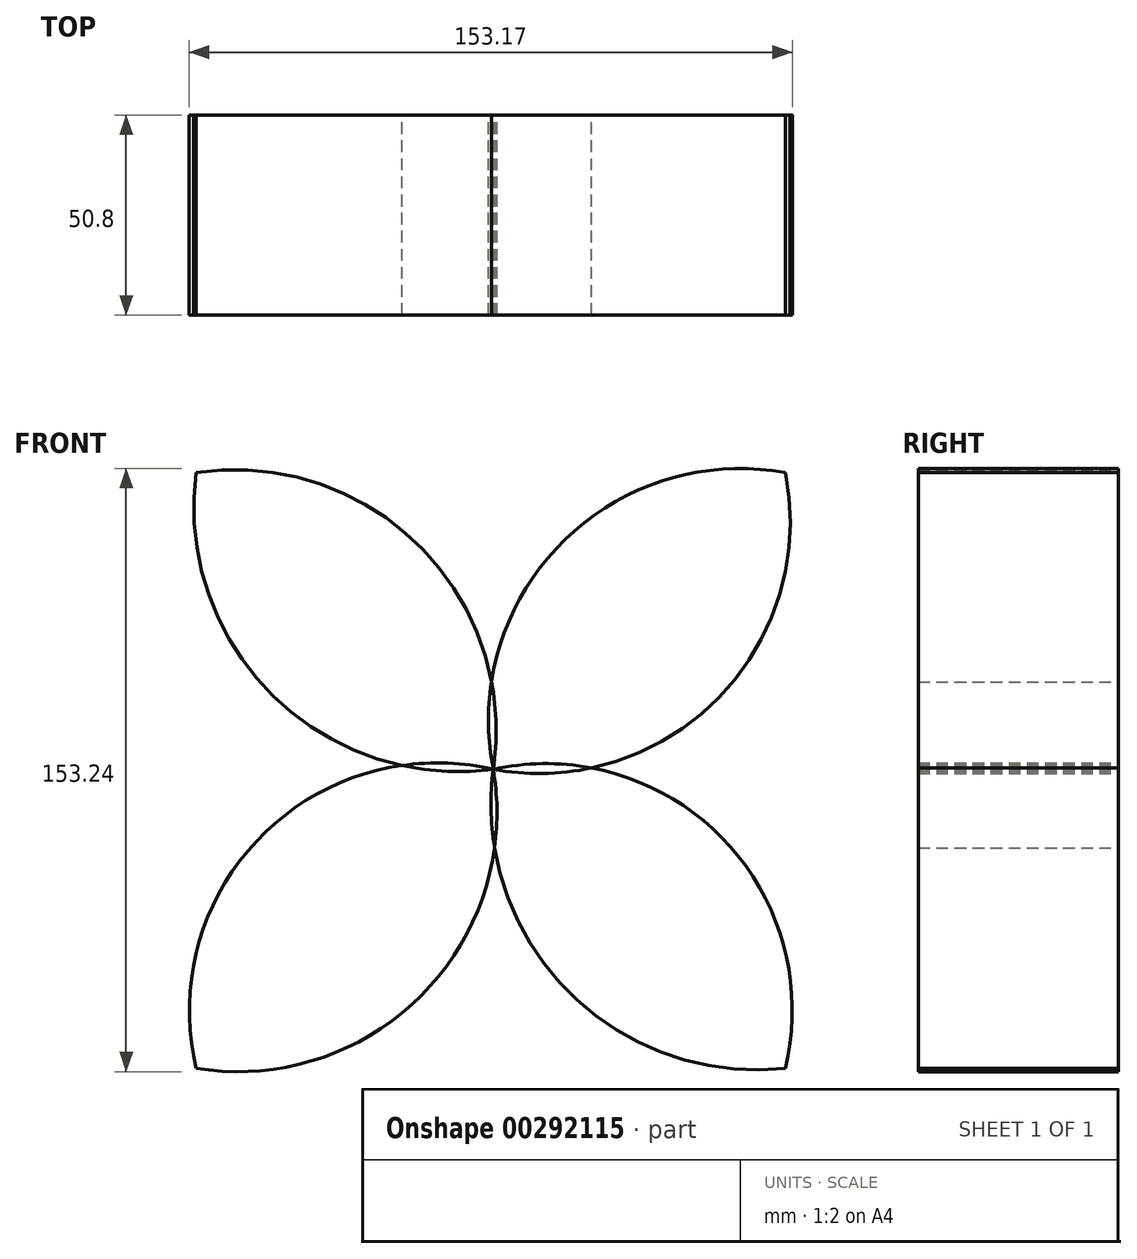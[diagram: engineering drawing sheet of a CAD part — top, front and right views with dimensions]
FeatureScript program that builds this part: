
annotation { "Feature Type Name" : "Feature", "Feature Type Description" : "" }
export const myFeature = defineFeature(function(context is Context, id is Id, definition is map)
    precondition{}
    {
        {
            var Q0;
            Q0=qCreatedBy(makeId("Front.planeOp"),FACE);
            var sketch = newSketch(context, id + "F0", { "sketchPlane" : qUnion([Q0])});
            skArc(sketch, "E0", {"start": v(-75.52, 75.41) * mm, "mid": v(-56.35, 19.09) * mm, "end": v(0, 0) * mm});
            skArc(sketch, "E1", {"start": v(0, 0) * mm, "mid": v(-18.76, 56.73) * mm, "end": v(-75.52, 75.41) * mm});
            skArc(sketch, "E2", {"start": v(74.17, 75.41) * mm, "mid": v(17.15, 57.3) * mm, "end": v(0, 0) * mm});
            skArc(sketch, "E3", {"start": v(0, 0) * mm, "mid": v(57.1, 18.02) * mm, "end": v(74.17, 75.41) * mm});
            skArc(sketch, "E4", {"start": v(74.17, -75.95) * mm, "mid": v(58.13, -17.42) * mm, "end": v(0, 0) * mm});
            skArc(sketch, "E5", {"start": v(0, 0) * mm, "mid": v(18.6, -56.02) * mm, "end": v(74.17, -75.95) * mm});
            skArc(sketch, "E6", {"start": v(-75.52, -75.95) * mm, "mid": v(-18.22, -57.4) * mm, "end": v(0, 0) * mm});
            skArc(sketch, "E7", {"start": v(0, 0) * mm, "mid": v(-58.9, -16.95) * mm, "end": v(-75.52, -75.95) * mm});
            skArc(sketch, "E8", {"start": v(-56.35, 19.09) * mm, "mid": v(-76.35, 2.29) * mm, "end": v(-56.35, -14.51) * mm});
            skPoint(sketch, "E8.endSnap0", {"position": v(-56.35, 19.09) * mm});
            skArc(sketch, "E9", {"start": v(57.1, -16.4) * mm, "mid": v(76.66, 0.81) * mm, "end": v(57.1, 18.02) * mm});
            skPoint(sketch, "E9.startSnap0", {"position": v(57.1, 18.02) * mm});
            skArc(sketch, "E10", {"start": v(-18.22, -57.4) * mm, "mid": v(0.89, -76.81) * mm, "end": v(20, -57.4) * mm});
            skPoint(sketch, "E10.endSnap0", {"position": v(-18.22, -57.4) * mm});
            skArc(sketch, "E11", {"start": v(16.6, 56.73) * mm, "mid": v(-1.08, 76.1) * mm, "end": v(-18.76, 56.73) * mm});
            skPoint(sketch, "E11.startSnap0", {"position": v(-18.76, 56.73) * mm});
            skSolve(sketch);
        }
        {
            var Q0;
            {var subQ0=sQuery(id+"F0.wireOp",EDGE,"E3");var subQ4=sQuery(id+"F0.wireOp",EDGE,"E2");var subQ8=makeQuery(id+"F0.imprint","INTERSECT",VERTEX,{"derivedFrom":[subQ4,subQ0]});Q0=makeQuery(id+"F0.imprint","IMPRINT",FACE,{"disambiguationData":[TD([[makeQuery(id+"F0.imprint","IMPRINT",EDGE,{"disambiguationData":[TD([[subQ8,-1.0]])],"derivedFrom":subQ4}),1.0]])]});}
            var Q1;
            {var subQ0=sQuery(id+"F0.wireOp",EDGE,"E1");var subQ4=sQuery(id+"F0.wireOp",EDGE,"E0");var subQ8=makeQuery(id+"F0.imprint","INTERSECT",VERTEX,{"derivedFrom":[subQ4,subQ0]});Q1=makeQuery(id+"F0.imprint","IMPRINT",FACE,{"disambiguationData":[TD([[makeQuery(id+"F0.imprint","IMPRINT",EDGE,{"disambiguationData":[TD([[subQ8,-1.0]])],"derivedFrom":subQ4}),1.0]])]});}
            var Q2;
            {var subQ0=sQuery(id+"F0.wireOp",EDGE,"E6");var subQ4=sQuery(id+"F0.wireOp",EDGE,"E7");var subQ5=makeQuery(id+"F0.imprint","INTERSECT",VERTEX,{"derivedFrom":[subQ0,subQ4]});Q2=makeQuery(id+"F0.imprint","IMPRINT",FACE,{"disambiguationData":[TD([[makeQuery(id+"F0.imprint","IMPRINT",EDGE,{"disambiguationData":[TD([[subQ5,-1.0]])],"derivedFrom":subQ0}),1.0]])]});}
            var Q3;
            {var subQ0=sQuery(id+"F0.wireOp",EDGE,"E5");var subQ4=sQuery(id+"F0.wireOp",EDGE,"E4");var subQ8=makeQuery(id+"F0.imprint","INTERSECT",VERTEX,{"derivedFrom":[subQ4,subQ0]});Q3=makeQuery(id+"F0.imprint","IMPRINT",FACE,{"disambiguationData":[TD([[makeQuery(id+"F0.imprint","IMPRINT",EDGE,{"disambiguationData":[TD([[subQ8,-1.0]])],"derivedFrom":subQ4}),1.0]])]});}
            extrude(context, id + "F1", {"entities" : qUnion([Q0, Q1, Q2, Q3]), "depth" : 50.8 * mm});
        }
    });
